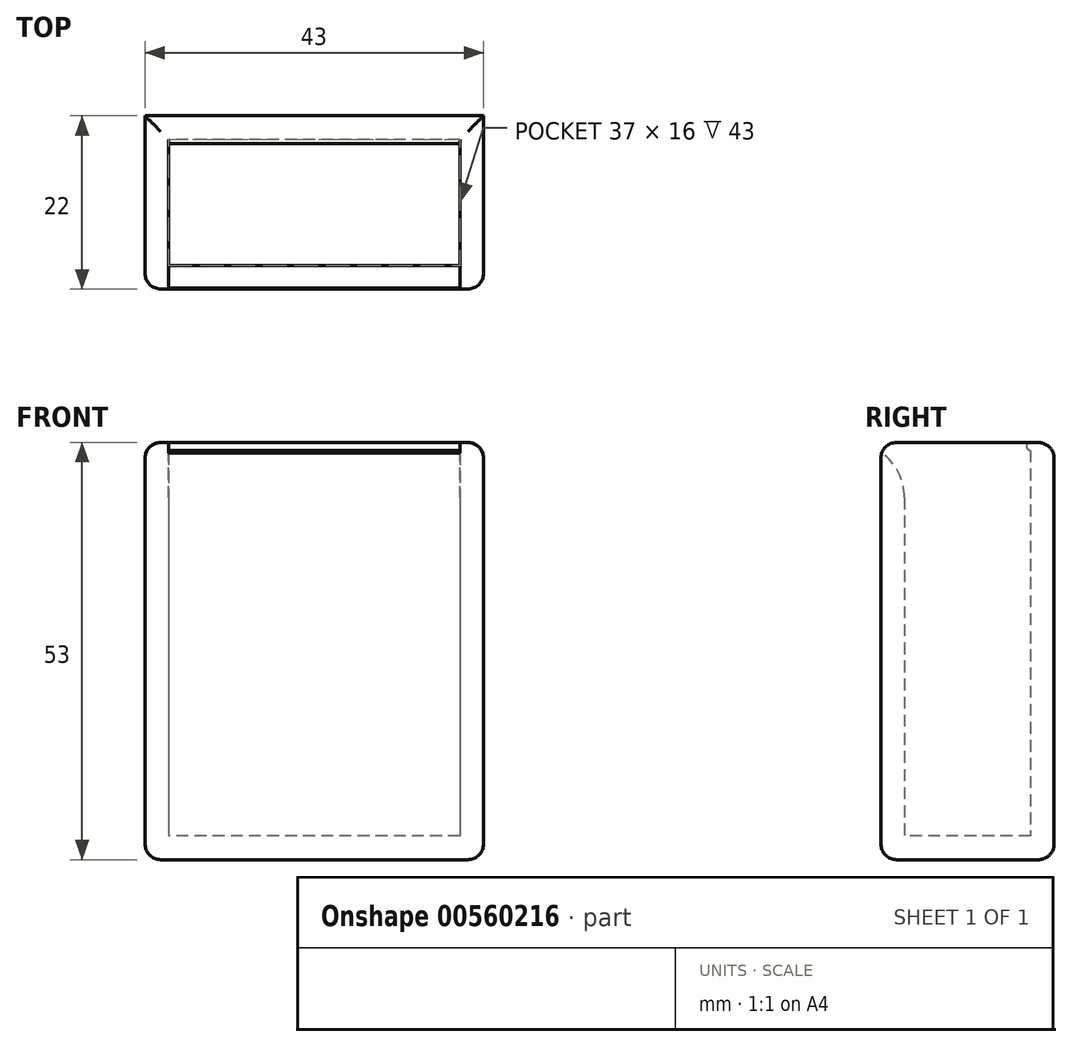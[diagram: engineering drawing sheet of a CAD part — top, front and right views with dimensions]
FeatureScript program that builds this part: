
annotation { "Feature Type Name" : "Feature", "Feature Type Description" : "" }
export const myFeature = defineFeature(function(context is Context, id is Id, definition is map)
    precondition{}
    {
        {
            var Q0;
            Q0=qCreatedBy(makeId("Top.planeOp"),FACE);
            var sketch = newSketch(context, id + "F0", { "sketchPlane" : qUnion([Q0])});
            skLineSegment(sketch, "E0.bottom", {"start": v(21.5, 11) * mm, "end": v(-21.5, 11) * mm});
            skLineSegment(sketch, "E0.top", {"start": v(21.5, -11) * mm, "end": v(-21.5, -11) * mm});
            skLineSegment(sketch, "E0.left", {"start": v(21.5, 11) * mm, "end": v(21.5, -11) * mm});
            skLineSegment(sketch, "E0.right", {"start": v(-21.5, 11) * mm, "end": v(-21.5, -11) * mm});
            skPoint(sketch, "E0.middle", {"position": v(0, 0) * mm});
            skSolve(sketch);
        }
        {
            var Q0;
            Q0=makeQuery(id+"F0.imprint","IMPRINT",FACE,{"disambiguationData":[TD([[makeQuery(id+"F0.imprint","IMPRINT",EDGE,{"derivedFrom":sQuery(id+"F0.wireOp",EDGE,"E0.bottom")}),1.0]])]});
            extrude(context, id + "F1", {"entities" : qUnion([Q0]), "depth" : 53 * mm, "offsetDistance" : 25 * mm});
        }
        {
            var Q0;
            Q0=makeQuery(id+"F1.opExtrude","CAP_FACE",FACE,{"disambiguationData":[OSD([sQuery(id+"F0.wireOp",EDGE,"E0.bottom"),sQuery(id+"F0.wireOp",EDGE,"E0.top"),sQuery(id+"F0.wireOp",EDGE,"E0.left"),sQuery(id+"F0.wireOp",EDGE,"E0.right")])],"isStart":false});
            shell(context, id + "F2", {"entities" : qUnion([Q0]), "thickness" : 3 * mm});
        }
        {
            var Q0;
            Q0=makeQuery(id+"F1.opExtrude","CAP_FACE",FACE,{"disambiguationData":[OSD([sQuery(id+"F0.wireOp",EDGE,"E0.bottom"),sQuery(id+"F0.wireOp",EDGE,"E0.top"),sQuery(id+"F0.wireOp",EDGE,"E0.left"),sQuery(id+"F0.wireOp",EDGE,"E0.right")])],"isStart":false});
            var sketch = newSketch(context, id + "F3", { "sketchPlane" : qUnion([Q0])});
            skLineSegment(sketch, "E1.bottom", {"start": v(18.5, 8) * mm, "end": v(-18.5, 8) * mm});
            skLineSegment(sketch, "E1.top", {"start": v(18.5, -8) * mm, "end": v(-18.5, -8) * mm});
            skLineSegment(sketch, "E1.left", {"start": v(18.5, 8) * mm, "end": v(18.5, -8) * mm});
            skLineSegment(sketch, "E1.right", {"start": v(-18.5, 8) * mm, "end": v(-18.5, -8) * mm});
            skPoint(sketch, "E1.middle", {"position": v(0, 0) * mm});
            skLineSegment(sketch, "E2.bottom", {"start": v(18.5, 7.5) * mm, "end": v(-18.5, 7.5) * mm});
            skLineSegment(sketch, "E2.top", {"start": v(18.5, -7.5) * mm, "end": v(-18.5, -7.5) * mm});
            skLineSegment(sketch, "E2.left", {"start": v(18.5, 7.5) * mm, "end": v(18.5, -7.5) * mm});
            skLineSegment(sketch, "E2.right", {"start": v(-18.5, 7.5) * mm, "end": v(-18.5, -7.5) * mm});
            skSolve(sketch);
        }
        {
            var Q0;
            Q0=makeQuery(id+"F3.imprint","IMPRINT",FACE,{"disambiguationData":[TD([[makeQuery(id+"F3.imprint","IMPRINT",EDGE,{"derivedFrom":sQuery(id+"F3.wireOp",EDGE,"E1.bottom")}),1.0]])]});
            extrude(context, id + "F4", {"entities" : qUnion([Q0]), "operationType" : NewBodyOperationType.ADD, "oppositeDirection" : true, "depth" : 1 * mm, "offsetDistance" : 25 * mm});
        }
        {
            var Q0;
            Q0=makeQuery(id+"F4.opExtrude","CAP_EDGE",EDGE,{"disambiguationData":[OSD([sQuery(id+"F3.wireOp",EDGE,"E2.bottom")])],"isStart":true});
            var Q1;
            Q1=makeQuery(id+"F4.opExtrude","CAP_EDGE",EDGE,{"disambiguationData":[OSD([sQuery(id+"F3.wireOp",EDGE,"E2.right")])],"isStart":true});
            var Q2;
            Q2=makeQuery(id+"F4.opExtrude","CAP_EDGE",EDGE,{"disambiguationData":[OSD([sQuery(id+"F3.wireOp",EDGE,"E2.right")])],"isStart":false});
            var Q3;
            Q3=makeQuery(id+"F4.opExtrude","CAP_EDGE",EDGE,{"disambiguationData":[OSD([sQuery(id+"F3.wireOp",EDGE,"E2.bottom")])],"isStart":false});
            var Q4;
            Q4=makeQuery(id+"F4.opExtrude","CAP_EDGE",EDGE,{"disambiguationData":[OSD([sQuery(id+"F3.wireOp",EDGE,"E2.top")])],"isStart":true});
            var Q5;
            Q5=makeQuery(id+"F4.opExtrude","CAP_EDGE",EDGE,{"disambiguationData":[OSD([sQuery(id+"F3.wireOp",EDGE,"E2.left")])],"isStart":true});
            var Q6;
            Q6=makeQuery(id+"F4.opExtrude","CAP_EDGE",EDGE,{"disambiguationData":[OSD([sQuery(id+"F3.wireOp",EDGE,"E2.left")])],"isStart":false});
            var Q7;
            Q7=makeQuery(id+"F4.opExtrude","CAP_EDGE",EDGE,{"disambiguationData":[OSD([sQuery(id+"F3.wireOp",EDGE,"E2.top")])],"isStart":false});
            fillet(context, id + "F5", {"entities" : qUnion([Q0, Q1, Q2, Q3, Q4, Q5, Q6, Q7]), "radius" : .5 * mm, "tangentPropagation" : true, "allowEdgeOverflow" : false});
        }
        {
            var Q0;
            Q0=makeQuery(id+"F1.opExtrude","SWEPT_EDGE",EDGE,{"disambiguationData":[OSD([sQuery(id+"F0.wireOp",EDGE,"E0.top"),sQuery(id+"F0.wireOp",EDGE,"E0.left")])]});
            var Q1;
            Q1=makeQuery(id+"F1.opExtrude","SWEPT_EDGE",EDGE,{"disambiguationData":[OSD([sQuery(id+"F0.wireOp",EDGE,"E0.top"),sQuery(id+"F0.wireOp",EDGE,"E0.right")])]});
            var Q2;
            Q2=makeQuery(id+"F1.opExtrude","CAP_FACE",FACE,{"disambiguationData":[OSD([sQuery(id+"F0.wireOp",EDGE,"E0.bottom"),sQuery(id+"F0.wireOp",EDGE,"E0.top"),sQuery(id+"F0.wireOp",EDGE,"E0.left"),sQuery(id+"F0.wireOp",EDGE,"E0.right")])],"isStart":true});
            var Q3;
            Q3=makeQuery(id+"F1.opExtrude","CAP_EDGE",EDGE,{"disambiguationData":[OSD([sQuery(id+"F0.wireOp",EDGE,"E0.right")])],"isStart":false});
            var Q4;
            Q4=makeQuery(id+"F1.opExtrude","CAP_EDGE",EDGE,{"disambiguationData":[OSD([sQuery(id+"F0.wireOp",EDGE,"E0.bottom")])],"isStart":false});
            var Q5;
            Q5=makeQuery(id+"F1.opExtrude","CAP_EDGE",EDGE,{"disambiguationData":[OSD([sQuery(id+"F0.wireOp",EDGE,"E0.left")])],"isStart":false});
            var Q6;
            Q6=makeQuery(id+"F1.opExtrude","CAP_EDGE",EDGE,{"disambiguationData":[OSD([sQuery(id+"F0.wireOp",EDGE,"E0.top")])],"isStart":false});
            fillet(context, id + "F6", {"entities" : qUnion([Q0, Q1, Q2, Q3, Q4, Q5, Q6]), "radius" : 2 * mm, "tangentPropagation" : true, "allowEdgeOverflow" : false});
        }
        {
            var Q0;
            {var subQ0=sQuery(id+"F0.wireOp",EDGE,"E0.top");Q0=makeQuery(id+"F2.opShell","OFFSET_EDGE",EDGE,{"disambiguationData":[OSD([subQ0]),TDD([makeQuery(id+"F1.opExtrude","CAP_EDGE",EDGE,{"disambiguationData":[OSD([subQ0])],"isStart":false})])]});}
            fillet(context, id + "F7", {"entities" : qUnion([Q0]), "radius" : 7 * mm, "tangentPropagation" : true, "allowEdgeOverflow" : false});
        }
    });
